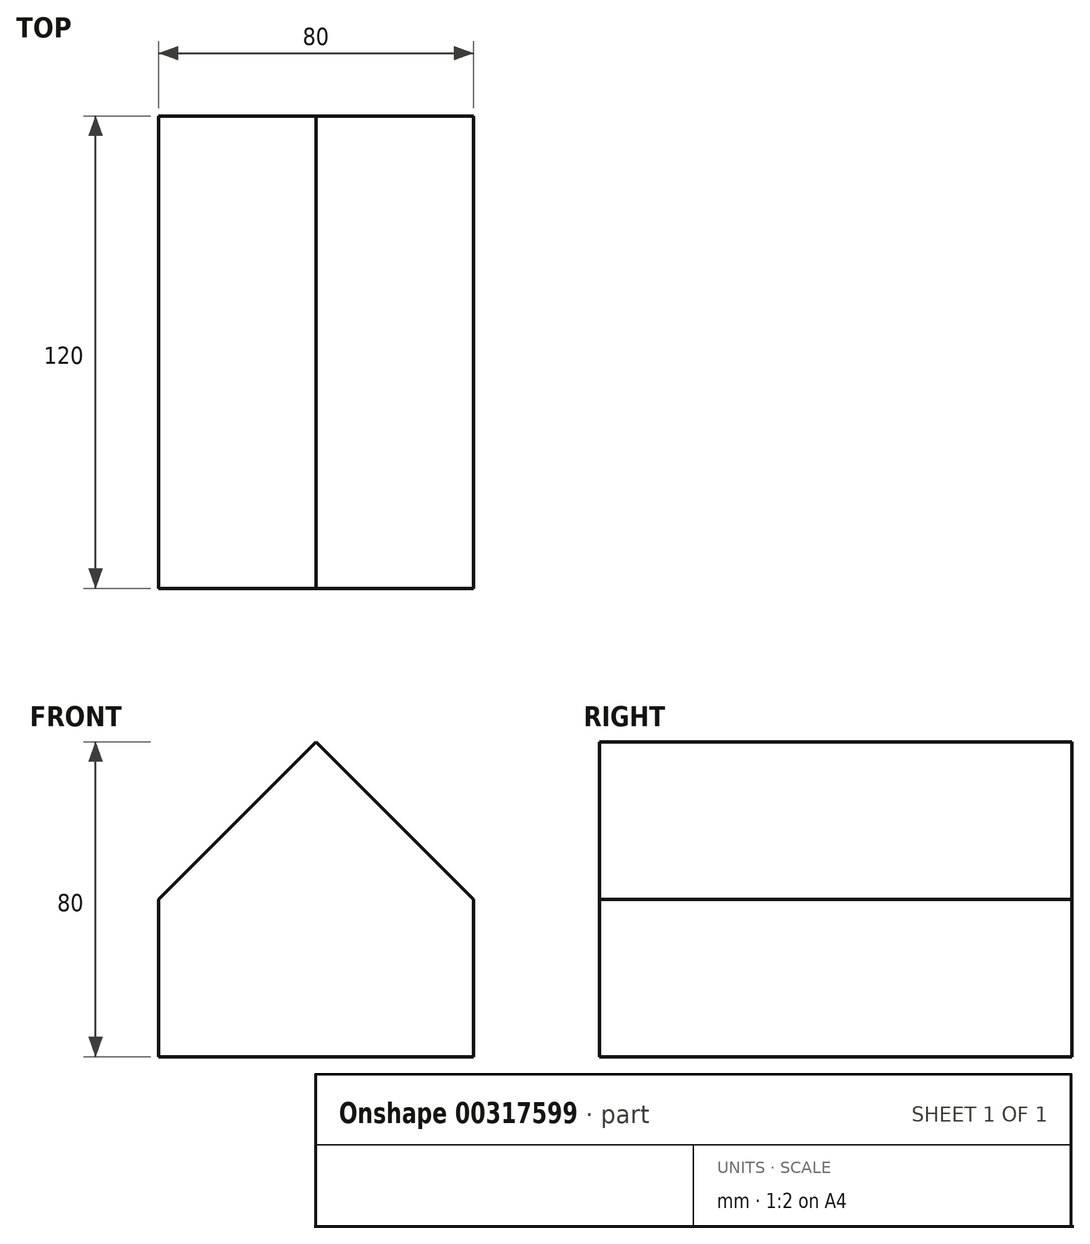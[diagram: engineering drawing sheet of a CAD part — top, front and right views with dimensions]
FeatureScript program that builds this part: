
annotation { "Feature Type Name" : "Feature", "Feature Type Description" : "" }
export const myFeature = defineFeature(function(context is Context, id is Id, definition is map)
    precondition{}
    {
        {
            var Q0;
            Q0=qCreatedBy(makeId("Front.planeOp"),FACE);
            var sketch = newSketch(context, id + "F0", { "sketchPlane" : qUnion([Q0])});
            skLineSegment(sketch, "E0", {"start": v(-40, 0) * mm, "end": v(0, 0) * mm});
            skLineSegment(sketch, "E1", {"start": v(0, 0) * mm, "end": v(40, 0) * mm});
            skLineSegment(sketch, "E2", {"start": v(-40, 0) * mm, "end": v(-40, 40) * mm});
            skLineSegment(sketch, "E3", {"start": v(40, 0) * mm, "end": v(40, 40) * mm});
            skLineSegment(sketch, "E4", {"start": v(-40, 40) * mm, "end": v(40, 40) * mm});
            skPoint(sketch, "E5.endSnap0", {"position": v(0, 40) * mm});
            skLineSegment(sketch, "E6", {"start": v(0, 40) * mm, "end": v(0, 80) * mm});
            skLineSegment(sketch, "E7", {"start": v(-40, 40) * mm, "end": v(0, 80) * mm});
            skLineSegment(sketch, "E8", {"start": v(40, 40) * mm, "end": v(0, 80) * mm});
            skSolve(sketch);
        }
        {
            var Q0;
            Q0 = qSketchRegion(id + "F0", true);
            extrude(context, id + "F1", {"entities" : qUnion([Q0]), "depth" : 120 * mm});
        }
    });
